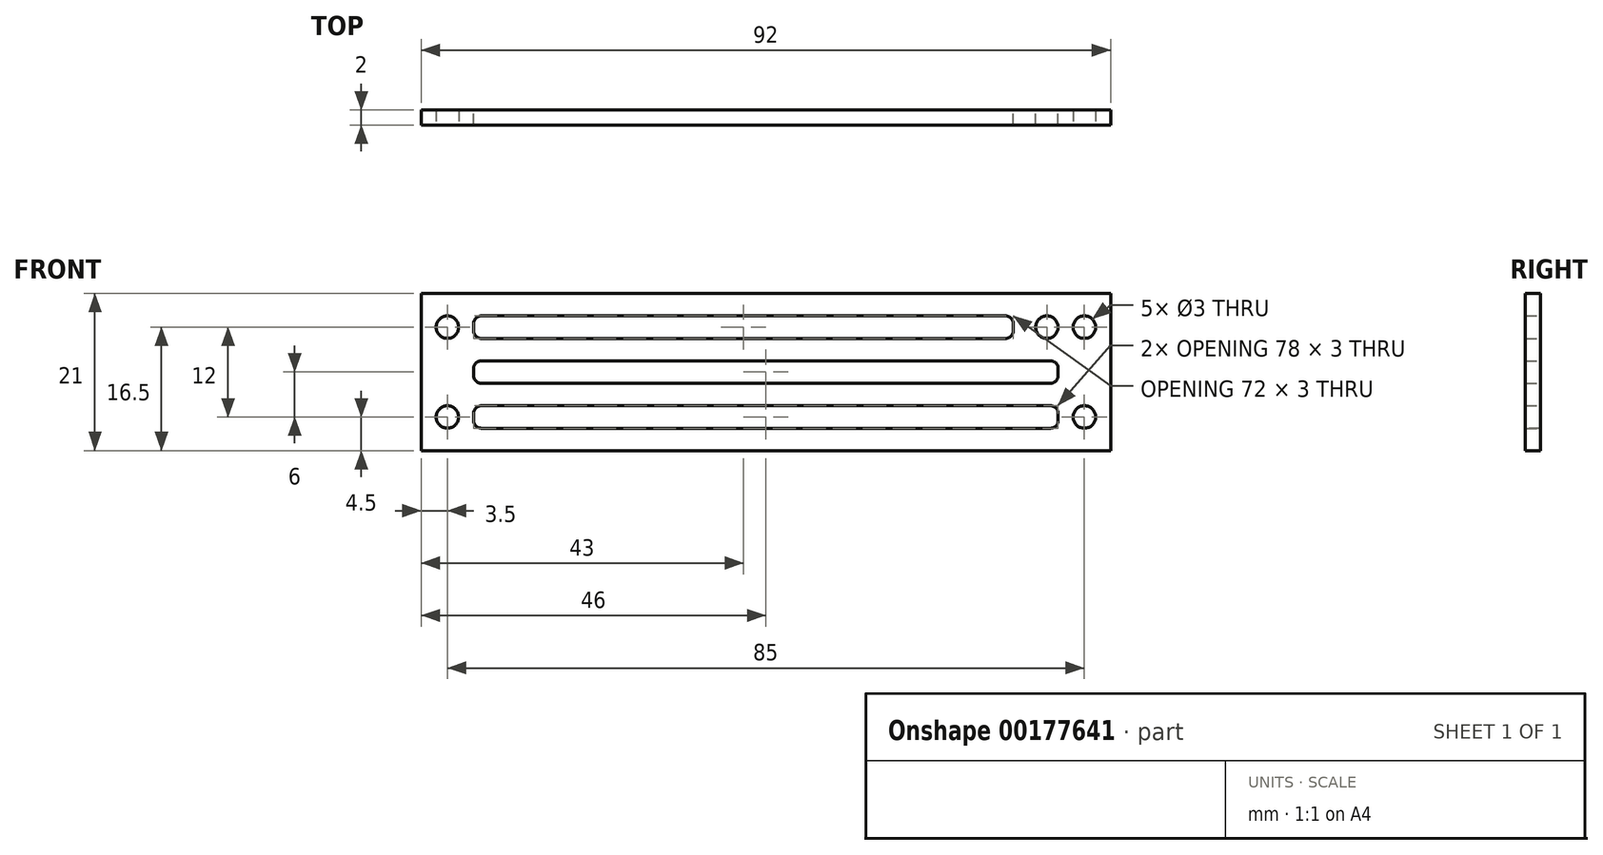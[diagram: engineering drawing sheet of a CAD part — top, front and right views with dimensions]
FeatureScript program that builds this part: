
annotation { "Feature Type Name" : "Feature", "Feature Type Description" : "" }
export const myFeature = defineFeature(function(context is Context, id is Id, definition is map)
    precondition{}
    {
        {
            var Q0;
            Q0=qCreatedBy(makeId("Front.planeOp"),FACE);
            var sketch = newSketch(context, id + "F0", { "sketchPlane" : qUnion([Q0])});
            skLineSegment(sketch, "E0.bottom", {"start": v(42, 10.5) * mm, "end": v(-42, 10.5) * mm});
            skLineSegment(sketch, "E0.top", {"start": v(42, -10.5) * mm, "end": v(-42, -10.5) * mm});
            skLineSegment(sketch, "E0.left", {"start": v(42, 10.5) * mm, "end": v(42, -10.5) * mm});
            skLineSegment(sketch, "E0.right", {"start": v(-42, 10.5) * mm, "end": v(-42, -10.5) * mm});
            skPoint(sketch, "E0.middle", {"position": v(0, 0) * mm});
            skLineSegment(sketch, "E1.bottom", {"start": v(39, -4.5) * mm, "end": v(-39, -4.5) * mm});
            skLineSegment(sketch, "E1.top", {"start": v(39, -7.5) * mm, "end": v(-39, -7.5) * mm});
            skLineSegment(sketch, "E1.left", {"start": v(39, -4.5) * mm, "end": v(39, -7.5) * mm});
            skLineSegment(sketch, "E1.right", {"start": v(-39, -4.5) * mm, "end": v(-39, -7.5) * mm});
            skPoint(sketch, "E1.middle", {"position": v(0, -6) * mm});
            skLineSegment(sketch, "E2.bottom", {"start": v(39, 1.5) * mm, "end": v(-39, 1.5) * mm});
            skLineSegment(sketch, "E2.top", {"start": v(39, -1.5) * mm, "end": v(-39, -1.5) * mm});
            skLineSegment(sketch, "E2.left", {"start": v(39, 1.5) * mm, "end": v(39, -1.5) * mm});
            skLineSegment(sketch, "E2.right", {"start": v(-39, 1.5) * mm, "end": v(-39, -1.5) * mm});
            skLineSegment(sketch, "E3.bottom", {"start": v(-39, 7.5) * mm, "end": v(33, 7.5) * mm});
            skLineSegment(sketch, "E3.top", {"start": v(-39, 4.5) * mm, "end": v(33, 4.5) * mm});
            skLineSegment(sketch, "E3.left", {"start": v(-39, 7.5) * mm, "end": v(-39, 4.5) * mm});
            skLineSegment(sketch, "E3.right", {"start": v(33, 7.5) * mm, "end": v(33, 4.5) * mm});
            skCircle(sketch, "E4", {"center": v(37.5, 6) * mm, "radius": 1.5 * mm});
            skSolve(sketch);
        }
        {
            var Q0;
            Q0=qSketchRegion(id+"F0",true);
            extrude(context, id + "F1", {"entities" : qUnion([Q0]), "depth" : 2 * mm});
        }
        {
            var Q0;
            Q0=makeQuery(id+"F1.opExtrude","SWEPT_FACE",FACE,{"disambiguationData":[OSD([sQuery(id+"F0.wireOp",EDGE,"E0.left")])]});
            var sketch = newSketch(context, id + "F2", { "sketchPlane" : qUnion([Q0])});
            skLineSegment(sketch, "E5.bottom", {"start": v(-2, 10.5) * mm, "end": v(0, 10.5) * mm});
            skLineSegment(sketch, "E5.top", {"start": v(-2, -10.5) * mm, "end": v(0, -10.5) * mm});
            skLineSegment(sketch, "E5.left", {"start": v(-2, 10.5) * mm, "end": v(-2, -10.5) * mm});
            skLineSegment(sketch, "E5.right", {"start": v(0, 10.5) * mm, "end": v(0, -10.5) * mm});
            skSolve(sketch);
        }
        {
            var Q0;
            Q0=qSketchRegion(id+"F2",true);
            extrude(context, id + "F3", {"entities" : qUnion([Q0]), "operationType" : NewBodyOperationType.ADD, "depth" : 5 * mm});
        }
        {
            var Q0;
            Q0=makeQuery(id+"F1.opExtrude","SWEPT_FACE",FACE,{"disambiguationData":[OSD([sQuery(id+"F0.wireOp",EDGE,"E0.right")])]});
            var sketch = newSketch(context, id + "F4", { "sketchPlane" : qUnion([Q0])});
            skLineSegment(sketch, "E6.bottom", {"start": v(0, 10.5) * mm, "end": v(2, 10.5) * mm});
            skLineSegment(sketch, "E6.top", {"start": v(0, -10.5) * mm, "end": v(2, -10.5) * mm});
            skLineSegment(sketch, "E6.left", {"start": v(0, 10.5) * mm, "end": v(0, -10.5) * mm});
            skLineSegment(sketch, "E6.right", {"start": v(2, 10.5) * mm, "end": v(2, -10.5) * mm});
            skSolve(sketch);
        }
        {
            var Q0;
            Q0=qSketchRegion(id+"F4",true);
            extrude(context, id + "F5", {"entities" : qUnion([Q0]), "operationType" : NewBodyOperationType.ADD, "depth" : 5 * mm});
        }
        {
            var Q0;
            Q0=makeQuery(id+"F5.boolean.opBoolean","MERGE",FACE,{"derivedFrom":[makeQuery(id+"F3.boolean.opBoolean","MERGE",FACE,{"derivedFrom":[makeQuery(id+"F1.opExtrude","CAP_FACE",FACE,{"disambiguationData":[OSD([sQuery(id+"F0.wireOp",EDGE,"E0.bottom"),sQuery(id+"F0.wireOp",EDGE,"E0.top"),sQuery(id+"F0.wireOp",EDGE,"E0.left"),sQuery(id+"F0.wireOp",EDGE,"E0.right"),sQuery(id+"F0.wireOp",EDGE,"E1.bottom"),sQuery(id+"F0.wireOp",EDGE,"E1.top"),sQuery(id+"F0.wireOp",EDGE,"E1.left"),sQuery(id+"F0.wireOp",EDGE,"E1.right"),sQuery(id+"F0.wireOp",EDGE,"E2.bottom"),sQuery(id+"F0.wireOp",EDGE,"E2.top"),sQuery(id+"F0.wireOp",EDGE,"E2.left"),sQuery(id+"F0.wireOp",EDGE,"E2.right"),sQuery(id+"F0.wireOp",EDGE,"E3.bottom"),sQuery(id+"F0.wireOp",EDGE,"E3.top"),sQuery(id+"F0.wireOp",EDGE,"E3.left"),sQuery(id+"F0.wireOp",EDGE,"E3.right"),sQuery(id+"F0.wireOp",EDGE,"E4")])],"isStart":false}),makeQuery(id+"F3.opExtrude","SWEPT_FACE",FACE,{"disambiguationData":[OSD([sQuery(id+"F2.wireOp",EDGE,"E5.left")])]})]}),makeQuery(id+"F5.opExtrude","SWEPT_FACE",FACE,{"disambiguationData":[OSD([sQuery(id+"F4.wireOp",EDGE,"E6.right")])]})]});
            var sketch = newSketch(context, id + "F6", { "sketchPlane" : qUnion([Q0])});
            skCircle(sketch, "E7", {"center": v(-42.5, 6) * mm, "radius": 1.5 * mm});
            skCircle(sketch, "E8", {"center": v(-42.5, -6) * mm, "radius": 1.5 * mm});
            skCircle(sketch, "E9", {"center": v(42.5, 6) * mm, "radius": 1.5 * mm});
            skCircle(sketch, "E10", {"center": v(42.5, -6) * mm, "radius": 1.5 * mm});
            skSolve(sketch);
        }
        {
            var Q0;
            Q0=qSketchRegion(id+"F6",true);
            extrude(context, id + "F7", {"entities" : qUnion([Q0]), "operationType" : NewBodyOperationType.REMOVE, "oppositeDirection" : true, "depth" : 25 * mm});
        }
        {
            var Q0;
            Q0=makeQuery(id+"F1.opExtrude","SWEPT_EDGE",EDGE,{"disambiguationData":[OSD([sQuery(id+"F0.wireOp",EDGE,"E3.bottom"),sQuery(id+"F0.wireOp",EDGE,"E3.left")])]});
            var Q1;
            Q1=makeQuery(id+"F1.opExtrude","SWEPT_EDGE",EDGE,{"disambiguationData":[OSD([sQuery(id+"F0.wireOp",EDGE,"E2.bottom"),sQuery(id+"F0.wireOp",EDGE,"E2.right")])]});
            var Q2;
            Q2=makeQuery(id+"F1.opExtrude","SWEPT_EDGE",EDGE,{"disambiguationData":[OSD([sQuery(id+"F0.wireOp",EDGE,"E1.bottom"),sQuery(id+"F0.wireOp",EDGE,"E1.right")])]});
            var Q3;
            Q3=makeQuery(id+"F1.opExtrude","SWEPT_EDGE",EDGE,{"disambiguationData":[OSD([sQuery(id+"F0.wireOp",EDGE,"E3.top"),sQuery(id+"F0.wireOp",EDGE,"E3.left")])]});
            var Q4;
            Q4=makeQuery(id+"F1.opExtrude","SWEPT_EDGE",EDGE,{"disambiguationData":[OSD([sQuery(id+"F0.wireOp",EDGE,"E2.top"),sQuery(id+"F0.wireOp",EDGE,"E2.right")])]});
            var Q5;
            Q5=makeQuery(id+"F1.opExtrude","SWEPT_EDGE",EDGE,{"disambiguationData":[OSD([sQuery(id+"F0.wireOp",EDGE,"E1.top"),sQuery(id+"F0.wireOp",EDGE,"E1.right")])]});
            var Q6;
            Q6=makeQuery(id+"F1.opExtrude","SWEPT_EDGE",EDGE,{"disambiguationData":[OSD([sQuery(id+"F0.wireOp",EDGE,"E3.bottom"),sQuery(id+"F0.wireOp",EDGE,"E3.right")])]});
            var Q7;
            Q7=makeQuery(id+"F1.opExtrude","SWEPT_EDGE",EDGE,{"disambiguationData":[OSD([sQuery(id+"F0.wireOp",EDGE,"E2.bottom"),sQuery(id+"F0.wireOp",EDGE,"E2.left")])]});
            var Q8;
            Q8=makeQuery(id+"F1.opExtrude","SWEPT_EDGE",EDGE,{"disambiguationData":[OSD([sQuery(id+"F0.wireOp",EDGE,"E1.bottom"),sQuery(id+"F0.wireOp",EDGE,"E1.left")])]});
            var Q9;
            Q9=makeQuery(id+"F1.opExtrude","SWEPT_EDGE",EDGE,{"disambiguationData":[OSD([sQuery(id+"F0.wireOp",EDGE,"E1.top"),sQuery(id+"F0.wireOp",EDGE,"E1.left")])]});
            var Q10;
            Q10=makeQuery(id+"F1.opExtrude","SWEPT_EDGE",EDGE,{"disambiguationData":[OSD([sQuery(id+"F0.wireOp",EDGE,"E2.top"),sQuery(id+"F0.wireOp",EDGE,"E2.left")])]});
            var Q11;
            Q11=makeQuery(id+"F1.opExtrude","SWEPT_EDGE",EDGE,{"disambiguationData":[OSD([sQuery(id+"F0.wireOp",EDGE,"E3.top"),sQuery(id+"F0.wireOp",EDGE,"E3.right")])]});
            fillet(context, id + "F8", {"entities" : qUnion([Q0, Q1, Q2, Q3, Q4, Q5, Q6, Q7, Q8, Q9, Q10, Q11]), "radius" : 1 * mm, "tangentPropagation" : true, "allowEdgeOverflow" : false});
        }
        {
            var Q0;
            Q0=makeQuery(id+"F5.boolean.opBoolean","MERGE",FACE,{"derivedFrom":[makeQuery(id+"F3.boolean.opBoolean","MERGE",FACE,{"derivedFrom":[makeQuery(id+"F1.opExtrude","CAP_FACE",FACE,{"disambiguationData":[OSD([sQuery(id+"F0.wireOp",EDGE,"E0.bottom"),sQuery(id+"F0.wireOp",EDGE,"E0.top"),sQuery(id+"F0.wireOp",EDGE,"E0.left"),sQuery(id+"F0.wireOp",EDGE,"E0.right"),sQuery(id+"F0.wireOp",EDGE,"E1.bottom"),sQuery(id+"F0.wireOp",EDGE,"E1.top"),sQuery(id+"F0.wireOp",EDGE,"E1.left"),sQuery(id+"F0.wireOp",EDGE,"E1.right"),sQuery(id+"F0.wireOp",EDGE,"E2.bottom"),sQuery(id+"F0.wireOp",EDGE,"E2.top"),sQuery(id+"F0.wireOp",EDGE,"E2.left"),sQuery(id+"F0.wireOp",EDGE,"E2.right"),sQuery(id+"F0.wireOp",EDGE,"E3.bottom"),sQuery(id+"F0.wireOp",EDGE,"E3.top"),sQuery(id+"F0.wireOp",EDGE,"E3.left"),sQuery(id+"F0.wireOp",EDGE,"E3.right"),sQuery(id+"F0.wireOp",EDGE,"E4")])],"isStart":false}),makeQuery(id+"F3.opExtrude","SWEPT_FACE",FACE,{"disambiguationData":[OSD([sQuery(id+"F2.wireOp",EDGE,"E5.left")])]})]}),makeQuery(id+"F5.opExtrude","SWEPT_FACE",FACE,{"disambiguationData":[OSD([sQuery(id+"F4.wireOp",EDGE,"E6.right")])]})]});
            var sketch = newSketch(context, id + "F9", { "sketchPlane" : qUnion([Q0])});
            skLineSegment(sketch, "E11.bottom", {"start": v(-47, 10.5) * mm, "end": v(-46, 10.5) * mm});
            skLineSegment(sketch, "E11.top", {"start": v(-47, -10.5) * mm, "end": v(-46, -10.5) * mm});
            skLineSegment(sketch, "E11.left", {"start": v(-47, 10.5) * mm, "end": v(-47, -10.5) * mm});
            skLineSegment(sketch, "E11.right", {"start": v(-46, 10.5) * mm, "end": v(-46, -10.5) * mm});
            skLineSegment(sketch, "E12.bottom", {"start": v(47, 10.5) * mm, "end": v(46, 10.5) * mm});
            skLineSegment(sketch, "E12.top", {"start": v(47, -10.5) * mm, "end": v(46, -10.5) * mm});
            skLineSegment(sketch, "E12.left", {"start": v(47, 10.5) * mm, "end": v(47, -10.5) * mm});
            skLineSegment(sketch, "E12.right", {"start": v(46, 10.5) * mm, "end": v(46, -10.5) * mm});
            skSolve(sketch);
        }
        {
            var Q0;
            Q0 = qSketchRegion(id + "F9", true);
            extrude(context, id + "F10", {"entities" : qUnion([Q0]), "operationType" : NewBodyOperationType.REMOVE, "oppositeDirection" : true, "depth" : 25 * mm});
        }
    });
